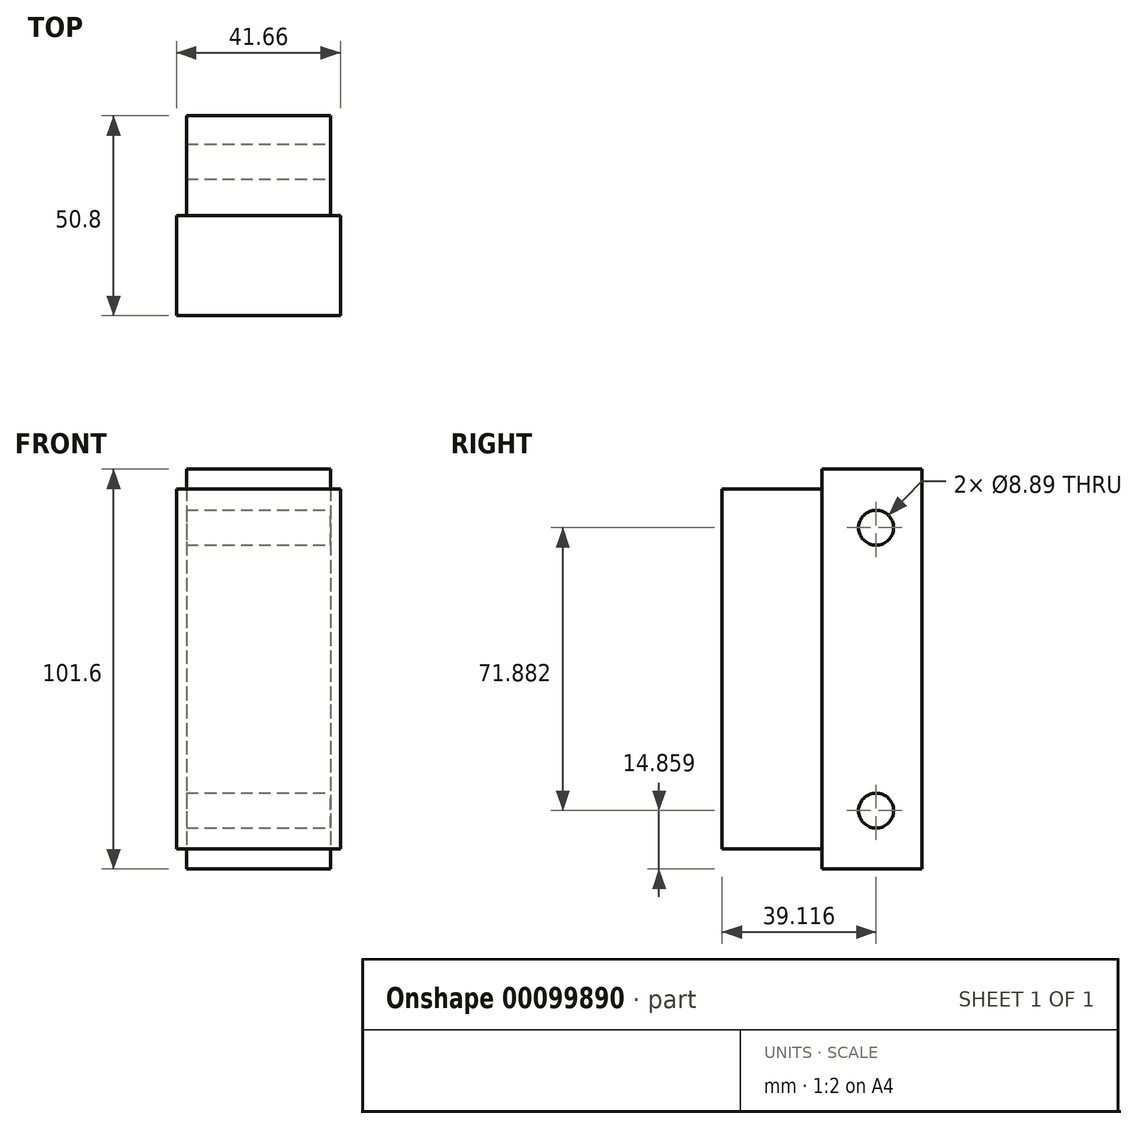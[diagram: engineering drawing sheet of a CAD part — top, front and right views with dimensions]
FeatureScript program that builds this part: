
annotation { "Feature Type Name" : "Feature", "Feature Type Description" : "" }
export const myFeature = defineFeature(function(context is Context, id is Id, definition is map)
    precondition{}
    {
        {
            var Q0;
            Q0=qCreatedBy(makeId("Front.planeOp"),FACE);
            var sketch = newSketch(context, id + "F0", { "sketchPlane" : qUnion([Q0])});
            skLineSegment(sketch, "E0.bottom", {"start": v(-20.83, 45.72) * mm, "end": v(20.83, 45.72) * mm});
            skLineSegment(sketch, "E0.top", {"start": v(-20.83, -45.72) * mm, "end": v(20.83, -45.72) * mm});
            skLineSegment(sketch, "E0.left", {"start": v(-20.83, 45.72) * mm, "end": v(-20.83, -45.72) * mm});
            skLineSegment(sketch, "E0.right", {"start": v(20.83, 45.72) * mm, "end": v(20.83, -45.72) * mm});
            skSolve(sketch);
        }
        {
            var Q0;
            Q0 = qSketchRegion(id + "F0", true);
            extrude(context, id + "F1", {"entities" : qUnion([Q0]), "depth" : 25.4 * mm});
        }
        {
            var Q0;
            Q0=qCreatedBy(makeId("Front.planeOp"),FACE);
            var sketch = newSketch(context, id + "F2", { "sketchPlane" : qUnion([Q0])});
            skLineSegment(sketch, "E1.bottom", {"start": v(-18.29, 50.8) * mm, "end": v(18.29, 50.8) * mm});
            skLineSegment(sketch, "E1.top", {"start": v(-18.29, -50.8) * mm, "end": v(18.29, -50.8) * mm});
            skLineSegment(sketch, "E1.left", {"start": v(-18.29, 50.8) * mm, "end": v(-18.29, -50.8) * mm});
            skLineSegment(sketch, "E1.right", {"start": v(18.29, 50.8) * mm, "end": v(18.29, -50.8) * mm});
            skSolve(sketch);
        }
        {
            var Q0;
            Q0 = qSketchRegion(id + "F2", true);
            extrude(context, id + "F3", {"entities" : qUnion([Q0]), "operationType" : NewBodyOperationType.ADD, "oppositeDirection" : true, "depth" : 25.4 * mm});
        }
        {
            var Q0;
            Q0=makeQuery(id+"F3.opExtrude","SWEPT_FACE",FACE,{"disambiguationData":[OSD([sQuery(id+"F2.wireOp",EDGE,"E1.right")])]});
            var sketch = newSketch(context, id + "F4", { "sketchPlane" : qUnion([Q0])});
            skCircle(sketch, "E2", {"center": v(13.72, 35.94) * mm, "radius": 4.45 * mm});
            skCircle(sketch, "E3", {"center": v(13.72, -35.94) * mm, "radius": 4.45 * mm});
            skSolve(sketch);
        }
        {
            var Q0;
            Q0 = qSketchRegion(id + "F4", true);
            extrude(context, id + "F5", {"entities" : qUnion([Q0]), "operationType" : NewBodyOperationType.REMOVE, "endBound" : BoundingType.UP_TO_NEXT, "oppositeDirection" : true, "depth" : 25.4 * mm});
        }
    });
